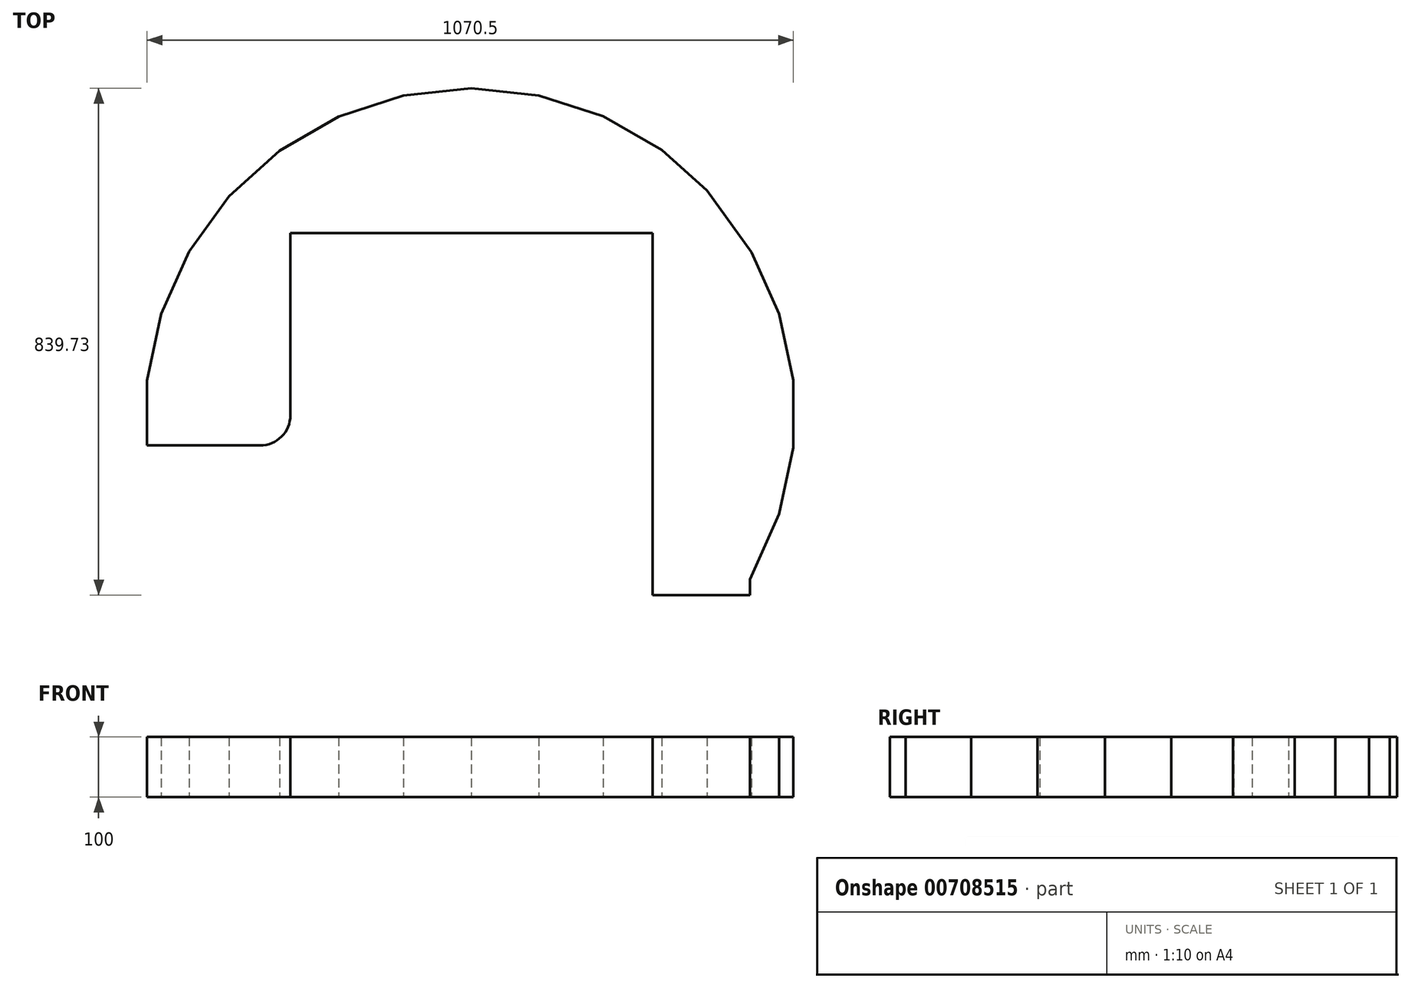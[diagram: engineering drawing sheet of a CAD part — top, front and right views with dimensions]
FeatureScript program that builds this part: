
annotation { "Feature Type Name" : "Feature", "Feature Type Description" : "" }
export const myFeature = defineFeature(function(context is Context, id is Id, definition is map)
    precondition{}
    {
        {
            var Q0;
            Q0=qCreatedBy(makeId("Top.planeOp"),FACE);
            var sketch = newSketch(context, id + "F0", { "sketchPlane" : qUnion([Q0])});
            skLineSegment(sketch, "E0.top", {"start": v(-250, 300) * mm, "end": v(250, 300) * mm});
            skLineSegment(sketch, "E0.left", {"start": v(-300, -2.1) * mm, "end": v(-300, 250) * mm});
            skLineSegment(sketch, "E0.right", {"start": v(300, -300) * mm, "end": v(300, 250) * mm});
            skPoint(sketch, "E0.middle", {"position": v(0, 0) * mm});
            skLineSegment(sketch, "E1", {"start": v(-537.3, -52.1) * mm, "end": v(-350, -52.1) * mm});
            skPoint(sketch, "E2.end.orphan", {"position": v(-300, -300) * mm});
            skLineSegment(sketch, "E3", {"start": v(300, -300) * mm, "end": v(461.55, -300) * mm});
            skPoint(sketch, "E4.visualSharp", {"position": v(-300, 300) * mm});
            skPoint(sketch, "E5.visualSharp", {"position": v(-300, -52.1) * mm});
            skPoint(sketch, "E6.visualSharp", {"position": v(300, 300) * mm});
            skLineSegment(sketch, "E7", {"start": v(-300, 250) * mm, "end": v(-300, 300) * mm});
            skLineSegment(sketch, "E8", {"start": v(-300, 300) * mm, "end": v(-250, 300) * mm});
            skLineSegment(sketch, "E9", {"start": v(250, 300) * mm, "end": v(300, 300) * mm});
            skLineSegment(sketch, "E10", {"start": v(300, 300) * mm, "end": v(300, 250) * mm});
            skLineSegment(sketch, "E11", {"start": v(-350, -52.1) * mm, "end": v(-350, -52.1) * mm});
            skLineSegment(sketch, "E12", {"start": v(-300, -2.1) * mm, "end": v(-300, -2.1) * mm});
            skLineSegment(sketch, "E13.0", {"start": v(509.88, -165.6) * mm, "end": v(461.55, -274.15) * mm});
            skLineSegment(sketch, "E13.1", {"start": v(533.2, -55.92) * mm, "end": v(509.88, -165.6) * mm});
            skLineSegment(sketch, "E13.2", {"start": v(533.16, 56.2) * mm, "end": v(533.2, -55.92) * mm});
            skLineSegment(sketch, "E13.3", {"start": v(509.8, 165.89) * mm, "end": v(533.16, 56.2) * mm});
            skLineSegment(sketch, "E13.4", {"start": v(464.16, 268.3) * mm, "end": v(509.8, 165.89) * mm});
            skLineSegment(sketch, "E13.5", {"start": v(390.06, 370.18) * mm, "end": v(464.16, 268.3) * mm});
            skLineSegment(sketch, "E13.6", {"start": v(315.2, 437.5) * mm, "end": v(390.06, 370.18) * mm});
            skLineSegment(sketch, "E13.7", {"start": v(218.04, 493.5) * mm, "end": v(315.2, 437.5) * mm});
            skLineSegment(sketch, "E13.8", {"start": v(-467.85, 269.18) * mm, "end": v(-401.6, 360.63) * mm});
            skLineSegment(sketch, "E13.9", {"start": v(-513.78, 166.02) * mm, "end": v(-467.85, 269.18) * mm});
            skLineSegment(sketch, "E13.10", {"start": v(-537.3, 55.32) * mm, "end": v(-513.78, 166.02) * mm});
            skLineSegment(sketch, "E13.12", {"start": v(-401.6, 360.63) * mm, "end": v(-317.8, 436.27) * mm});
            skLineSegment(sketch, "E13.13", {"start": v(-317.8, 436.27) * mm, "end": v(-220.1, 492.82) * mm});
            skLineSegment(sketch, "E13.14", {"start": v(-220.1, 492.82) * mm, "end": v(-112.79, 527.82) * mm});
            skLineSegment(sketch, "E13.15", {"start": v(-112.79, 527.82) * mm, "end": v(-0.53, 539.73) * mm});
            skLineSegment(sketch, "E13.16", {"start": v(-0.53, 539.73) * mm, "end": v(111.37, 528.07) * mm});
            skLineSegment(sketch, "E13.17", {"start": v(111.37, 528.07) * mm, "end": v(218.04, 493.5) * mm});
            skLineSegment(sketch, "E14", {"start": v(-537.3, 55.32) * mm, "end": v(-537.3, -52.1) * mm});
            skLineSegment(sketch, "E15", {"start": v(461.55, -274.15) * mm, "end": v(461.55, -300) * mm});
            skArc(sketch, "E16.filletArc", {"start": v(-350, -52.1) * mm, "mid": v(-314.64, -37.45) * mm, "end": v(-300, -2.1) * mm});
            skSolve(sketch);
        }
        {
            var Q0;
            Q0=qSketchRegion(id+"F0",true);
            extrude(context, id + "F1", {"entities" : qUnion([Q0]), "depth" : 100 * mm, "offsetDistance" : 25 * mm});
        }
    });
